# Revit family: Shower-Drain-KOHLER-K-75423T_1
name_source: partatom
category: Plumbing Fixtures
revit_build: Autodesk Revit 2017 (Build: 20160225_1515(x64)
units: mm (PartAtom-declared; Revit-internal decimal feet)

## family parameters
Cut with Voids When Loaded = No
Host = Face
OmniClass Number = 23.31.17.29
OmniClass Title = Shower Drains
Part Type = Normal
Room Calculation Point = No
Round Connector Dimension = Use Diameter
Shared = No

## types (1)
- CP-Polished Chrome
    ADA Compliant = No
    Assembly Code = D2010
    CW Connection = No
    Cold Water Inlet = Cold Water Inlet
    Date Modified = 10/19/2020
    Default Elevation = 0"
    Description = Large traffic is hidden.
    Drain Included = Yes
    Finish = Kohler-Metal-CP-Polished_Chrome
    HW Connection = No
    Height = 3 5/16"
    Hot Water Inlet = Hot Water Inlet
    Length = 23 5/8"
    Manufacturer = KOHLER Co.
    MasterFormat 1995 = 15410
    MasterFormat 2004 = 22.41.16
    Material = Premium Metal Construction
    Model = K-75423T-CP
    Product Documentation Link = https://files.kohler.com.cn
    Product Page URL = https://www.kohler.com.cn
    URL = http://www.kohler.com.cn
    Vent Connection = No
    Waste Connection = Yes
    Waste Water Outlet = Waste Water Outlet
    WaterSense Certified = No
    Width = 3 1/8"

## geometry (parser evidence)
native form markers: Sweep x4
no freeform markers — native parametric forms only
